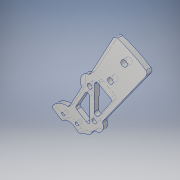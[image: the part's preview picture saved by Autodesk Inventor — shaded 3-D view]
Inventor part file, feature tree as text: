
AUTODESK INVENTOR PART (.ipt)
format: ipt  version: 2019 (Build 230136000, 136)  size: 203,264 bytes
history: native  units: in
note: dims shown in document units (in); Inventor stores cm internally (conversion verified against a paired STEP export)
features: extrude x4, sketch x4, other x3, fillet x1, reference x1
ambient origin geometry x8: Origin, YZ Plane, XZ Plane, XY Plane, X Axis, Y Axis, Z Axis, Center Point
bodies: Solid1 (feature_tree)
feature tree (13):
  extrude  "Extrusion1"  Depth=0.25in TaperAngle=0.0deg
  extrude  "Extrusion2"  Depth=0.25in
  extrude  "Extrusion3"  Depth=0.25in
  extrude  "Extrusion4"  Depth=0.25in TaperAngle=0.0deg
  fillet  "Fillet2"  Radius=0.25in
  sketch  "Sketch1"  dims[d1=1.5in d2=0.25in d3=0.0in]
  reference  "Reference1"
  sketch  "Sketch2"  dims[d4=0.25in d5=0.25in]
  sketch  "Sketch3"  dims[d6=0.25in d7=0.75in]
  sketch  "Sketch4"  dims[d8=0.125in d9=0.25in d10=0.0in d12=0.25in d13=0.25in d14=0.0in d15=0.5in d16=0.25in d17=0.0in d18=0.125in d19=0.0625in]
  parser-record x1  (decoder bookkeeping rows leaked as tree rows — omitted from the tree; the rows remain in map.json)
  other  "Wheel.iam"
  other  "Wall:1"
note: 1 file-system path scrubbed to <path> (originals preserved in map.json)
